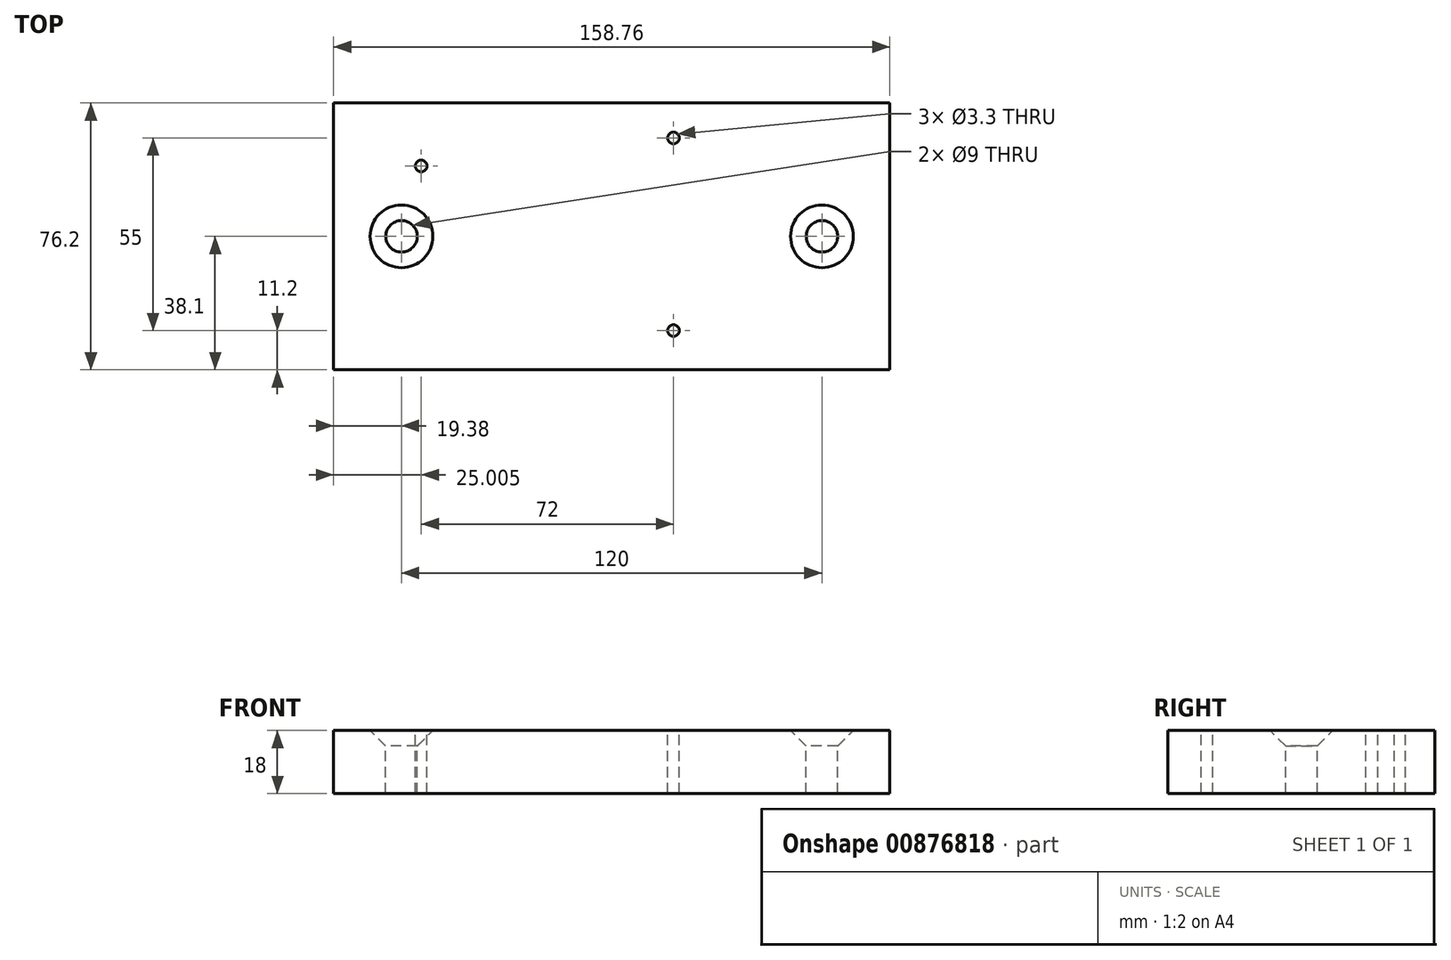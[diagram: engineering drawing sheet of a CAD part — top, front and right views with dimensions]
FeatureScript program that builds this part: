
annotation { "Feature Type Name" : "Feature", "Feature Type Description" : "" }
export const myFeature = defineFeature(function(context is Context, id is Id, definition is map)
    precondition{}
    {
        {
            var Q0;
            Q0=qCreatedBy(makeId("Top.planeOp"),FACE);
            var sketch = newSketch(context, id + "F0", { "sketchPlane" : qUnion([Q0])});
            skLineSegment(sketch, "E0.bottom", {"start": v(-79.38, 38.1) * mm, "end": v(79.38, 38.1) * mm});
            skLineSegment(sketch, "E0.top", {"start": v(-79.38, -38.1) * mm, "end": v(79.38, -38.1) * mm});
            skLineSegment(sketch, "E0.left", {"start": v(-79.38, 38.1) * mm, "end": v(-79.38, -38.1) * mm});
            skLineSegment(sketch, "E0.right", {"start": v(79.38, 38.1) * mm, "end": v(79.37, -38.1) * mm});
            skPoint(sketch, "E0.middle", {"position": v(0, 0) * mm});
            skSolve(sketch);
        }
        {
            var Q0;
            Q0 = qSketchRegion(id + "F0", true);
            extrude(context, id + "F1", {"entities" : qUnion([Q0]), "endBound" : BoundingType.SYMMETRIC, "depth" : 18 * mm, "offsetDistance" : 25.4 * mm});
        }
        {
            var Q0;
            Q0=makeQuery(id+"F1.opExtrude","CAP_FACE",FACE,{"disambiguationData":[OSD([sQuery(id+"F0.wireOp",EDGE,"E0.bottom"),sQuery(id+"F0.wireOp",EDGE,"E0.top"),sQuery(id+"F0.wireOp",EDGE,"E0.left"),sQuery(id+"F0.wireOp",EDGE,"E0.right")])],"isStart":false});
            var sketch = newSketch(context, id + "F2", { "sketchPlane" : qUnion([Q0])});
            skLineSegment(sketch, "E1", {"start": v(-129.93, 0) * mm, "end": v(143.62, 0) * mm, "construction": true});
            skLineSegment(sketch, "E2", {"start": v(0, 85.42) * mm, "end": v(0, -85.42) * mm, "construction": true});
            skLineSegment(sketch, "E3.0", {"start": v(-60, 85.42) * mm, "end": v(-60, -85.42) * mm, "construction": true});
            skPoint(sketch, "E4", {"position": v(-60, 0) * mm});
            skPoint(sketch, "E5.MirrorP", {"position": v(60, 0) * mm});
            skSolve(sketch);
        }
        {
            var Q0;
            Q0=sQuery(id+"F2.wireOp",VERTEX,"E4");
            var Q1;
            Q1=sQuery(id+"F2.wireOp",VERTEX,"E5.MirrorP");
            var Q2;
            Q2=makeQuery(id+"F1.opExtrude","SWEPT_BODY",BODY,{"disambiguationData":[OSD([sQuery(id+"F0.wireOp",EDGE,"E0.bottom"),sQuery(id+"F0.wireOp",EDGE,"E0.top"),sQuery(id+"F0.wireOp",EDGE,"E0.left"),sQuery(id+"F0.wireOp",EDGE,"E0.right")])]});
            hole(context, id + "F3", {"style" : HoleStyle.C_SINK, "endStyle" : HoleEndStyle.THROUGH, "standardTappedOrClearance" : lookupTablePath({ "fit" : "Normal", "standard" : "ISO", "size" : "M8", "type" : "Clearance" }), "standardBlindInLast" : lookupTablePath({ "fit" : "Normal", "standard" : "ISO", "size" : "M8", "type" : "Clearance" }), "holeDiameter" : 9 * mm, "cSinkDiameter" : 17.92 * mm, "cSinkAngle" : 90 * degree, "majorDiameter" : 5 * mm, "isTappedThrough" : true, "tappedDepth" : 12 * mm, "tapClearance" : 3, "locations" : qUnion([Q0, Q1]), "scope" : qUnion([Q2])});
        }
        {
            var Q0;
            Q0=makeQuery(id+"F1.opExtrude","CAP_FACE",FACE,{"disambiguationData":[OSD([sQuery(id+"F0.wireOp",EDGE,"E0.bottom"),sQuery(id+"F0.wireOp",EDGE,"E0.top"),sQuery(id+"F0.wireOp",EDGE,"E0.left"),sQuery(id+"F0.wireOp",EDGE,"E0.right")])],"isStart":false});
            var sketch = newSketch(context, id + "F4", { "sketchPlane" : qUnion([Q0])});
            skLineSegment(sketch, "E6.0", {"start": v(-54.37, 38.1) * mm, "end": v(-54.38, -38.1) * mm, "construction": true});
            skLineSegment(sketch, "E7.0", {"start": v(-79.38, 20.1) * mm, "end": v(79.38, 20.1) * mm, "construction": true});
            skPoint(sketch, "E8", {"position": v(-54.37, 20.1) * mm});
            skLineSegment(sketch, "E9.0", {"start": v(-79.38, 28.1) * mm, "end": v(79.38, 28.1) * mm, "construction": true});
            skLineSegment(sketch, "E10.0", {"start": v(17.63, 38.1) * mm, "end": v(17.62, -38.1) * mm, "construction": true});
            skPoint(sketch, "E11", {"position": v(17.63, 28.1) * mm});
            skLineSegment(sketch, "E12.0", {"start": v(-79.38, -26.9) * mm, "end": v(79.38, -26.9) * mm, "construction": true});
            skPoint(sketch, "E13", {"position": v(17.62, -26.9) * mm});
            skSolve(sketch);
        }
        {
            var Q0;
            Q0=sQuery(id+"F4.wireOp",VERTEX,"E8");
            var Q1;
            Q1=sQuery(id+"F4.wireOp",VERTEX,"E11");
            var Q2;
            Q2=sQuery(id+"F4.wireOp",VERTEX,"E13");
            var Q3;
            Q3=makeQuery(id+"F1.opExtrude","SWEPT_BODY",BODY,{"disambiguationData":[OSD([sQuery(id+"F0.wireOp",EDGE,"E0.bottom"),sQuery(id+"F0.wireOp",EDGE,"E0.top"),sQuery(id+"F0.wireOp",EDGE,"E0.left"),sQuery(id+"F0.wireOp",EDGE,"E0.right")])]});
            hole(context, id + "F5", {"style" : HoleStyle.SIMPLE, "endStyle" : HoleEndStyle.THROUGH, "standardTappedOrClearance" : lookupTablePath({ "standard" : "ISO", "engagement" : "75%", "pitch" : "0.7 mm", "size" : "M4", "type" : "Tapped" }), "standardBlindInLast" : lookupTablePath({ "standard" : "ISO", "engagement" : "75%", "pitch" : "0.7 mm", "size" : "M4", "type" : "Tapped" }), "holeDiameter" : 3.3 * mm, "majorDiameter" : 4 * mm, "showTappedDepth" : true, "isTappedThrough" : true, "tappedDepth" : 12 * mm, "tapClearance" : 3, "locations" : qUnion([Q0, Q1, Q2]), "scope" : qUnion([Q3])});
        }
    });
